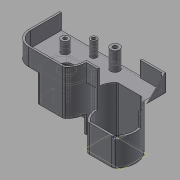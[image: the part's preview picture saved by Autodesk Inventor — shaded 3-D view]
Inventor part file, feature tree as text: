
AUTODESK INVENTOR PART (.ipt)
format: ipt  version: 2015 (Build 190159000, 159)  size: 287,744 bytes
history: native  units: mm
features: extrude x15, sketch x15, plane x15, reference x9
ambient origin geometry x8: Origin, YZ Plane, XZ Plane, XY Plane, X Axis, Y Axis, Z Axis, Center Point
bodies: Solid1 (feature_tree)
feature tree (54):
  extrude  "Extrusion1"  Depth=15.0mm TaperAngle=0.0deg
  sketch  "Sketch2"  dims[d3=15.0mm d4=0.0mm d8=1.0mm]
  plane  "Work Plane1"
  extrude  "Extrusion2"  Depth=1.0mm
  sketch  "Sketch3"  dims[d9=15.0mm d10=0.0mm d11=15.0mm d12=0.0mm]
  plane  "Work Plane2"
  extrude  "Extrusion4"  Depth=15.0mm TaperAngle=0.0deg
  sketch  "Sketch5"  dims[d19=1.0mm d20=0.0mm d29=8.5mm d30=0.0mm]
  plane  "Work Plane3"
  extrude  "Extrusion5"  Depth=1.0mm TaperAngle=0.0deg
  extrude  "Extrusion6"  Depth=8.5mm TaperAngle=0.0deg
  sketch  "Sketch6"  dims[d33=1.0mm d34=10.0mm d35=0.0mm]
  plane  "Work Plane4"
  extrude  "Extrusion7"  Depth=10.0mm TaperAngle=0.0deg
  sketch  "Sketch7"  dims[d36=10.0mm d37=0.0mm d43=10.0mm d44=0.0mm]
  plane  "Work Plane5"
  extrude  "Extrusion8"  Depth=10.0mm TaperAngle=0.0deg
  plane  "Work Plane6"
  plane  "Work Plane7"
  plane  "Work Plane8"
  plane  "Work Plane9"
  extrude  "Extrusion13"  Depth=3.5mm
  sketch  "Sketch13"  dims[d52=1.0mm d53=0.0mm d54=3.5mm]
  plane  "Work Plane10"
  extrude  "Extrusion14"  Depth=3.5mm
  sketch  "Sketch14"  dims[d55=5.0mm d56=1.0mm d57=0.0mm]
  plane  "Work Plane11"
  extrude  "Extrusion15"  Depth=1.0mm TaperAngle=0.0deg
  sketch  "Sketch15"  dims[d58=3.5mm d59=1.0mm d60=0.0mm]
  plane  "Work Plane12"
  plane  "Work Plane13"
  plane  "Work Plane14"
  extrude  "Extrusion18"  Depth=1.0mm TaperAngle=0.0deg
  sketch  "Sketch17"
  plane  "Work Plane15"
  extrude  "Extrusion19"  [1 undecoded]
  extrude  "Extrusion21"  [1 undecoded]
  extrude  "Extrusion22"  [1 undecoded]
  extrude  "Extrusion23"  [1 undecoded]
  sketch  "Sketch1"  dims[d0=1.0mm d1=15.0mm d2=0.0mm]
  sketch  "Sketch4"  dims[d14=1.0mm d15=0.0mm d17=1.0mm d18=0.0mm]
  reference  "Reference18"
  reference  "Reference19"
  sketch  "Sketch12"  dims[d45=10.0mm d46=0.0mm d51=3.5mm]
  reference  "Reference30"
  reference  "Reference31"
  reference  "Reference32"
  reference  "Reference36"
  sketch  "Sketch19"
  reference  "Reference38"
  sketch  "Sketch20"
  reference  "Reference39"
  sketch  "Sketch21"
  reference  "Reference40"
note: 4 required parameter values undecoded (feature->parameter linkage not recoverable at this tier; creation-order binding heuristic only, values carry confidence <= 0.55)
